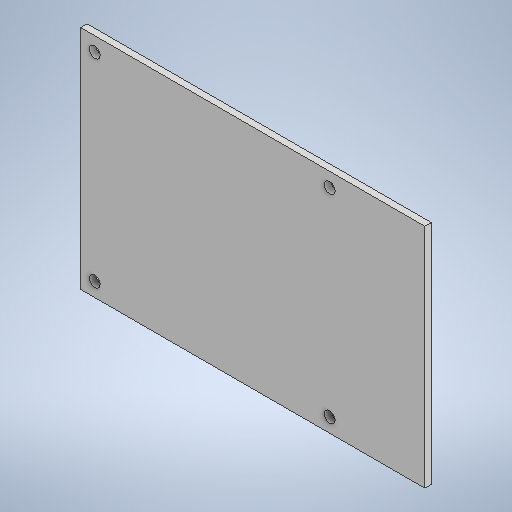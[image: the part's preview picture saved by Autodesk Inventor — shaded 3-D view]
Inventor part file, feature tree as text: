
AUTODESK INVENTOR PART (.ipt)
format: ipt  version: 2025 (Build 290162000, 162)  size: 216,064 bytes
history: native  units: in
note: dims shown in document units (in); Inventor stores cm internally (conversion verified against a paired STEP export)
features: other x1, extrude x1, sketch x1
ambient origin geometry x8: Origin, YZ Plane, XZ Plane, XY Plane, X Axis, Y Axis, Z Axis, Center Point
bodies: Body1 (feature_tree)
feature tree (3):
  other  "솔리드1"
  extrude  "돌출1"  Depth=3.3465in
  sketch  "스케치1"
